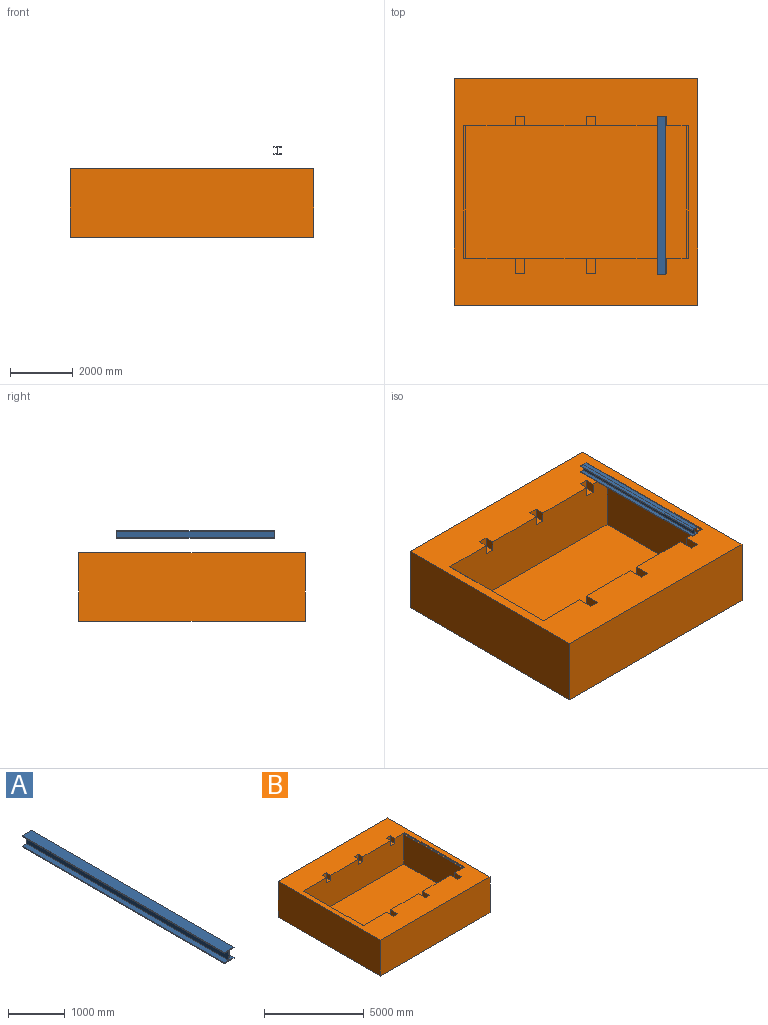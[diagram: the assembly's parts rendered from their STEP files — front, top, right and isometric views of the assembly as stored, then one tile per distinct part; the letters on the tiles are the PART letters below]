
ASSEMBLY  parts=2 mates=1
PART A: 14 faces, bbox 240x5035x240 mm
  f0: plane 5035x240mm, normal (0,0,1), area 1208400mm2, adj f1,f11,f12,f13
  f1: plane 5035x17mm, normal (-1,0,0), area 85595mm2, adj f0,f2,f12,f13
  f2: plane 5035x115mm, normal (0,0,-1), area 579025mm2, adj f1,f3,f12,f13
  f3: plane 5035x206mm, normal (-1,0,0), area 1037210mm2, adj f2,f4,f12,f13
  f4: plane 5035x115mm, normal (0,0,1), area 579025mm2, adj f3,f5,f12,f13
  f5: plane 5035x17mm, normal (-1,0,0), area 85595mm2, adj f4,f6,f12,f13
  f6: plane 5035x240mm, normal (0,0,-1), area 1208400mm2, adj f5,f7,f12,f13
  f7: plane 5035x17mm, normal (1,0,0), area 85595mm2, adj f6,f8,f12,f13
  f8: plane 5035x115mm, normal (0,0,1), area 579025mm2, adj f7,f9,f12,f13
  f9: plane 5035x206mm, normal (1,0,0), area 1037210mm2, adj f8,f10,f12,f13
  f10: plane 5035x115mm, normal (0,0,-1), area 579025mm2, adj f9,f11,f12,f13
  f11: plane 5035x17mm, normal (1,0,0), area 85595mm2, adj f0,f10,f12,f13
  f12: plane 240x240mm, normal (0,-1,0), area 10220mm2, adj f0,f1,f2,f3,f4,f5,f6,f7
  f13: plane 240x240mm, normal (0,1,0), area 10220mm2, adj f0,f1,f2,f3,f4,f5,f6,f7
PART B: 39 faces, bbox 7780x7235x2200 mm
  f0: plane 7780x7235mm, normal (0,0,1), area 25185000mm2, adj f1,f2,f4,f5,f11,f12,f13,f14
  f1: plane 7180x1900mm, normal (0,-1,0), area 13107400mm2, adj f0,f5,f6,f7,f8,f9,f10,f11
  f2: plane 7235x2200mm, normal (-1,0,0), area 15917000mm2, adj f0,f3,f13,f14
  f3: plane 7780x7235mm, normal (0,0,-1), area 56288300mm2, adj f2,f4,f13,f14
  f4: plane 7235x2200mm, normal (1,0,0), area 15917000mm2, adj f0,f3,f13,f14
  f5: plane 4235x70mm, normal (-1,0,0), area 296450mm2, adj f0,f1,f6,f12
  f6: plane 4235x70mm, normal (0,0,1), area 296450mm2, adj f1,f5,f7,f12
  f7: plane 4235x1830mm, normal (-1,0,0), area 7750050mm2, adj f1,f6,f8,f12
  f8: plane 7040x4235mm, normal (0,0,1), area 29814400mm2, adj f1,f7,f9,f12
  f9: plane 4235x1830mm, normal (1,0,0), area 7750050mm2, adj f1,f8,f10,f12
  f10: plane 4235x70mm, normal (0,0,1), area 296450mm2, adj f1,f9,f11,f12
  f11: plane 4235x70mm, normal (1,0,0), area 296450mm2, adj f0,f1,f10,f12
  f12: plane 7180x1900mm, normal (0,1,0), area 13107400mm2, adj f0,f5,f6,f7,f8,f9,f10,f11
  f13: plane 7780x2200mm, normal (0,-1,0), area 17116000mm2, adj f0,f2,f3,f4
  f14: plane 7780x2200mm, normal (0,1,0), area 17116000mm2, adj f0,f2,f3,f4
  f15: plane 320x300mm, normal (1,0,0), area 96000mm2, adj f0,f1,f17,f18
  f16: plane 320x300mm, normal (-1,0,0), area 96000mm2, adj f0,f1,f17,f18
  f17: plane 320x290mm, normal (0,-1,0), area 92800mm2, adj f0,f15,f16,f18
  f18: plane 300x290mm, normal (0,0,1), area 87000mm2, adj f1,f15,f16,f17
  f19: plane 500x320mm, normal (1,0,0), area 160000mm2, adj f0,f12,f20,f22
  f20: plane 320x290mm, normal (0,1,0), area 92800mm2, adj f0,f19,f21,f22
  f21: plane 500x320mm, normal (-1,0,0), area 160000mm2, adj f0,f12,f20,f22
  f22: plane 500x290mm, normal (0,0,1), area 145000mm2, adj f12,f19,f20,f21
  f23: plane 500x320mm, normal (1,0,0), area 160000mm2, adj f0,f12,f24,f26
  f24: plane 320x290mm, normal (0,1,0), area 92800mm2, adj f0,f23,f25,f26
  f25: plane 500x320mm, normal (-1,0,0), area 160000mm2, adj f0,f12,f24,f26
  f26: plane 500x290mm, normal (0,0,1), area 145000mm2, adj f12,f23,f24,f25
  f27: plane 320x300mm, normal (1,0,0), area 96000mm2, adj f0,f1,f29,f30
  f28: plane 320x300mm, normal (-1,0,0), area 96000mm2, adj f0,f1,f29,f30
  f29: plane 320x290mm, normal (0,-1,0), area 92800mm2, adj f0,f27,f28,f30
  f30: plane 300x290mm, normal (0,0,1), area 87000mm2, adj f1,f27,f28,f29
  f31: plane 500x320mm, normal (1,0,0), area 160000mm2, adj f0,f12,f32,f34
  f32: plane 320x290mm, normal (0,1,0), area 92800mm2, adj f0,f31,f33,f34
  f33: plane 500x320mm, normal (-1,0,0), area 160000mm2, adj f0,f12,f32,f34
  f34: plane 500x290mm, normal (0,0,1), area 145000mm2, adj f12,f31,f32,f33
  f35: plane 320x300mm, normal (1,0,0), area 96000mm2, adj f0,f1,f37,f38
  f36: plane 320x300mm, normal (-1,0,0), area 96000mm2, adj f0,f1,f37,f38
  f37: plane 320x290mm, normal (0,-1,0), area 92800mm2, adj f0,f35,f36,f38
  f38: plane 300x290mm, normal (0,0,1), area 87000mm2, adj f1,f35,f36,f37
PLACE A t=(4531.2,1995.5,1196.43)mm
PLACE B t=(-1159.06,1708,-1484.1)mm
MATE parallel B.f38 <-> A.f6  axis (0,0,1) through (4511.2,1858,176.43)mm
